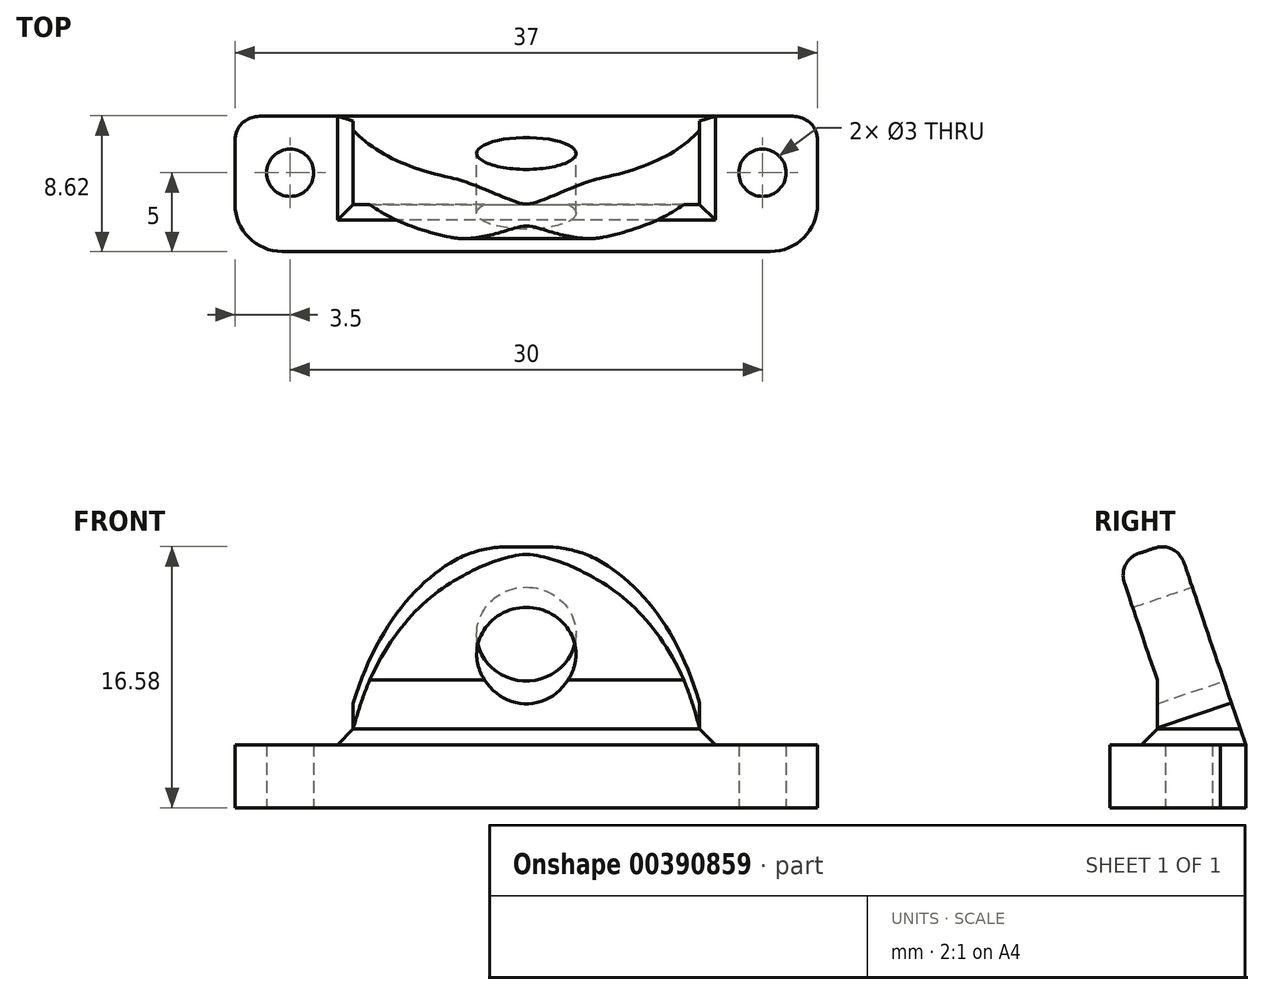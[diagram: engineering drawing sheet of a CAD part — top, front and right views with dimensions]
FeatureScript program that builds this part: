
annotation { "Feature Type Name" : "Feature", "Feature Type Description" : "" }
export const myFeature = defineFeature(function(context is Context, id is Id, definition is map)
    precondition{}
    {
        {
            var Q0;
            Q0=qCreatedBy(makeId("Top.planeOp"),FACE);
            var sketch = newSketch(context, id + "F0", { "sketchPlane" : qUnion([Q0])});
            skLineSegment(sketch, "E0.top", {"start": v(-15, 0) * mm, "end": v(15, 0) * mm});
            skPoint(sketch, "E0.middle", {"position": v(0, 0) * mm});
            skCircle(sketch, "E1", {"center": v(-15, 0) * mm, "radius": 1.5 * mm});
            skCircle(sketch, "E2", {"center": v(15, 0) * mm, "radius": 1.5 * mm});
            skLineSegment(sketch, "E3.bottom", {"start": v(-15.5, -5) * mm, "end": v(15.5, -5) * mm});
            skLineSegment(sketch, "E3.left", {"start": v(-18.5, -2) * mm, "end": v(-18.5, 2) * mm});
            skLineSegment(sketch, "E3.right", {"start": v(18.5, -2) * mm, "end": v(18.5, 2) * mm});
            skPoint(sketch, "E4.visualSharp", {"position": v(-18.5, 5) * mm});
            skPoint(sketch, "E5.visualSharp", {"position": v(-18.5, -5) * mm});
            skArc(sketch, "E5.filletArc", {"start": v(-18.5, -2) * mm, "mid": v(-17.62, -4.12) * mm, "end": v(-15.5, -5) * mm});
            skPoint(sketch, "E6.visualSharp", {"position": v(18.5, 5) * mm});
            skPoint(sketch, "E7.visualSharp", {"position": v(18.5, -5) * mm});
            skArc(sketch, "E7.filletArc", {"start": v(15.5, -5) * mm, "mid": v(17.62, -4.12) * mm, "end": v(18.5, -2) * mm});
            skLineSegment(sketch, "E8", {"start": v(-16.4, 3.62) * mm, "end": v(16.4, 3.62) * mm});
            skFitSpline(sketch, "E9", {"points": [v(-18.5, 2) * mm, v(-16.4, 3.62) * mm], "startDerivative": vector(0.1, 4.65) * mm, "endDerivative": vector(2.26, 0) * mm});
            skFitSpline(sketch, "E10.MirrorCS", {"points": [v(18.5, 2) * mm, v(16.4, 3.62) * mm], "startDerivative": vector(-0.1, 4.65) * mm, "endDerivative": vector(-2.26, 0) * mm});
            skSolve(sketch);
        }
        {
            var Q0;
            Q0 = qSketchRegion(id + "F0", true);
            extrude(context, id + "F1", {"entities" : qUnion([Q0]), "depth" : 3 * mm, "offsetDistance" : 25 * mm});
        }
        {
            var Q0;
            Q0=qCreatedBy(makeId("Right.planeOp"),FACE);
            var sketch = newSketch(context, id + "F2", { "sketchPlane" : qUnion([Q0])});
            skLineSegment(sketch, "E11", {"start": v(-2.01, 2.9) * mm, "end": v(-2.01, 7.12) * mm});
            skLineSegment(sketch, "E12", {"start": v(-2.01, 7.12) * mm, "end": v(-4.1, 13.28) * mm});
            skLineSegment(sketch, "E13", {"start": v(-3.16, 15.18) * mm, "end": v(-2.21, 15.5) * mm});
            skLineSegment(sketch, "E14", {"start": v(-0.3, 14.56) * mm, "end": v(3.6, 3) * mm});
            skLineSegment(sketch, "E15", {"start": v(-2.01, 2.9) * mm, "end": v(3.6, 3) * mm});
            skPoint(sketch, "E16.visualSharp", {"position": v(-4.58, 14.7) * mm});
            skArc(sketch, "E16.filletArc", {"start": v(-3.16, 15.18) * mm, "mid": v(-4.02, 14.42) * mm, "end": v(-4.1, 13.28) * mm});
            skPoint(sketch, "E17.visualSharp", {"position": v(-0.79, 15.98) * mm});
            skArc(sketch, "E17.filletArc", {"start": v(-0.3, 14.56) * mm, "mid": v(-1.06, 15.42) * mm, "end": v(-2.21, 15.5) * mm});
            skSolve(sketch);
        }
        {
            var Q0;
            Q0 = qSketchRegion(id + "F2", true);
            extrude(context, id + "F3", {"entities" : qUnion([Q0]), "operationType" : NewBodyOperationType.ADD, "depth" : 11 * mm, "offsetDistance" : 25 * mm, "hasSecondDirection" : true, "secondDirectionOppositeDirection" : true, "secondDirectionDepth" : 11 * mm});
        }
        {
            var Q0;
            Q0=makeQuery(id+"F3.opExtrude","SWEPT_FACE",FACE,{"disambiguationData":[OSD([sQuery(id+"F2.wireOp",EDGE,"E14")])]});
            var sketch = newSketch(context, id + "F4", { "sketchPlane" : qUnion([Q0])});
            skCircle(sketch, "E18", {"center": v(0, 9.1) * mm, "radius": 3.15 * mm});
            skSolve(sketch);
        }
        {
            var Q0;
            Q0 = qSketchRegion(id + "F4", true);
            extrude(context, id + "F5", {"entities" : qUnion([Q0]), "operationType" : NewBodyOperationType.REMOVE, "oppositeDirection" : true, "depth" : 6 * mm, "offsetDistance" : 25 * mm});
        }
        {
            var Q0;
            Q0=makeQuery(id+"F3.opExtrude","SWEPT_FACE",FACE,{"disambiguationData":[OSD([sQuery(id+"F2.wireOp",EDGE,"E12")])]});
            var sketch = newSketch(context, id + "F6", { "sketchPlane" : qUnion([Q0])});
            skFitSpline(sketch, "E19", {"points": [v(-11, 4.47) * mm, v(11, 4.45) * mm], "startDerivative": vector(11.5, 42.5) * mm, "endDerivative": vector(12.9, -44.76) * mm});
            skLineSegment(sketch, "E20", {"start": v(0, 12.25) * mm, "end": v(0, 19.91) * mm, "construction": true});
            skFitSpline(sketch, "E21.MirrorCS", {"points": [v(11, 4.47) * mm, v(-11, 4.45) * mm], "startDerivative": vector(-11.5, 42.5) * mm, "endDerivative": vector(-12.9, -44.76) * mm});
            skLineSegment(sketch, "E22", {"start": v(-11, 4.45) * mm, "end": v(-12.83, 15.02) * mm});
            skLineSegment(sketch, "E23", {"start": v(-12.83, 15.02) * mm, "end": v(-4.1, 22.02) * mm});
            skLineSegment(sketch, "E24", {"start": v(-4.1, 22.02) * mm, "end": v(10.02, 21.11) * mm});
            skLineSegment(sketch, "E25", {"start": v(10.02, 21.11) * mm, "end": v(15.68, 15.2) * mm});
            skLineSegment(sketch, "E26", {"start": v(15.68, 15.2) * mm, "end": v(11, 4.47) * mm});
            skSolve(sketch);
        }
        {
            var Q0;
            Q0 = qSketchRegion(id + "F6", true);
            extrude(context, id + "F7", {"entities" : qUnion([Q0]), "operationType" : NewBodyOperationType.REMOVE, "oppositeDirection" : true, "depth" : 25 * mm, "offsetDistance" : 25 * mm, "hasSecondDirection" : true, "secondDirectionOppositeDirection" : false, "secondDirectionDepth" : 4 * mm});
        }
        {
            var Q0;
            Q0=makeQuery(id+"F3.boolean.opBoolean","INTERSECT",EDGE,{"derivedFrom":[makeQuery(id+"F1.opExtrude","CAP_FACE",FACE,{"disambiguationData":[OSD([sQuery(id+"F0.wireOp",EDGE,"E1"),sQuery(id+"F0.wireOp",EDGE,"E2"),sQuery(id+"F0.wireOp",EDGE,"E3.bottom"),sQuery(id+"F0.wireOp",EDGE,"E3.left"),sQuery(id+"F0.wireOp",EDGE,"E3.right"),sQuery(id+"F0.wireOp",EDGE,"E5.filletArc"),sQuery(id+"F0.wireOp",EDGE,"E7.filletArc"),sQuery(id+"F0.wireOp",EDGE,"E8"),sQuery(id+"F0.wireOp",EDGE,"E9"),sQuery(id+"F0.wireOp",EDGE,"E10.MirrorCS")])],"isStart":false}),makeQuery(id+"F3.opExtrude","CAP_FACE",FACE,{"disambiguationData":[OSD([sQuery(id+"F2.wireOp",EDGE,"E11"),sQuery(id+"F2.wireOp",EDGE,"E12"),sQuery(id+"F2.wireOp",EDGE,"E13"),sQuery(id+"F2.wireOp",EDGE,"E14"),sQuery(id+"F2.wireOp",EDGE,"E15"),sQuery(id+"F2.wireOp",EDGE,"E16.filletArc"),sQuery(id+"F2.wireOp",EDGE,"E17.filletArc")])],"isStart":false})]});
            var Q1;
            Q1=makeQuery(id+"F3.boolean.opBoolean","INTERSECT",EDGE,{"derivedFrom":[makeQuery(id+"F1.opExtrude","CAP_FACE",FACE,{"disambiguationData":[OSD([sQuery(id+"F0.wireOp",EDGE,"E1"),sQuery(id+"F0.wireOp",EDGE,"E2"),sQuery(id+"F0.wireOp",EDGE,"E3.bottom"),sQuery(id+"F0.wireOp",EDGE,"E3.left"),sQuery(id+"F0.wireOp",EDGE,"E3.right"),sQuery(id+"F0.wireOp",EDGE,"E5.filletArc"),sQuery(id+"F0.wireOp",EDGE,"E7.filletArc"),sQuery(id+"F0.wireOp",EDGE,"E8"),sQuery(id+"F0.wireOp",EDGE,"E9"),sQuery(id+"F0.wireOp",EDGE,"E10.MirrorCS")])],"isStart":false}),makeQuery(id+"F3.opExtrude","CAP_FACE",FACE,{"disambiguationData":[OSD([sQuery(id+"F2.wireOp",EDGE,"E11"),sQuery(id+"F2.wireOp",EDGE,"E12"),sQuery(id+"F2.wireOp",EDGE,"E13"),sQuery(id+"F2.wireOp",EDGE,"E14"),sQuery(id+"F2.wireOp",EDGE,"E15"),sQuery(id+"F2.wireOp",EDGE,"E16.filletArc"),sQuery(id+"F2.wireOp",EDGE,"E17.filletArc")])],"isStart":true})]});
            chamfer(context, id + "F8", {"entities" : qUnion([Q0, Q1]), "width" : 1 * mm, "tangentPropagation" : true});
        }
        {
            var Q0;
            Q0=makeQuery(id+"F3.boolean.opBoolean","INTERSECT",EDGE,{"derivedFrom":[makeQuery(id+"F1.opExtrude","CAP_FACE",FACE,{"disambiguationData":[OSD([sQuery(id+"F0.wireOp",EDGE,"E1"),sQuery(id+"F0.wireOp",EDGE,"E2"),sQuery(id+"F0.wireOp",EDGE,"E3.bottom"),sQuery(id+"F0.wireOp",EDGE,"E3.left"),sQuery(id+"F0.wireOp",EDGE,"E3.right"),sQuery(id+"F0.wireOp",EDGE,"E5.filletArc"),sQuery(id+"F0.wireOp",EDGE,"E7.filletArc"),sQuery(id+"F0.wireOp",EDGE,"E8"),sQuery(id+"F0.wireOp",EDGE,"E9"),sQuery(id+"F0.wireOp",EDGE,"E10.MirrorCS")])],"isStart":false}),makeQuery(id+"F3.opExtrude","SWEPT_FACE",FACE,{"disambiguationData":[OSD([sQuery(id+"F2.wireOp",EDGE,"E11")])]})]});
            chamfer(context, id + "F9", {"entities" : qUnion([Q0]), "width" : 1 * mm, "tangentPropagation" : true});
        }
        {
            var Q0;
            Q0=makeQuery(id+"F1.opExtrude","CAP_FACE",FACE,{"disambiguationData":[OSD([sQuery(id+"F0.wireOp",EDGE,"E1"),sQuery(id+"F0.wireOp",EDGE,"E2"),sQuery(id+"F0.wireOp",EDGE,"E3.bottom"),sQuery(id+"F0.wireOp",EDGE,"E3.left"),sQuery(id+"F0.wireOp",EDGE,"E3.right"),sQuery(id+"F0.wireOp",EDGE,"E5.filletArc"),sQuery(id+"F0.wireOp",EDGE,"E7.filletArc"),sQuery(id+"F0.wireOp",EDGE,"E8"),sQuery(id+"F0.wireOp",EDGE,"E9"),sQuery(id+"F0.wireOp",EDGE,"E10.MirrorCS")])],"isStart":true});
            extrude(context, id + "F10", {"entities" : qUnion([Q0]), "operationType" : NewBodyOperationType.ADD, "depth" : 1 * mm, "offsetDistance" : 25 * mm});
        }
    });
